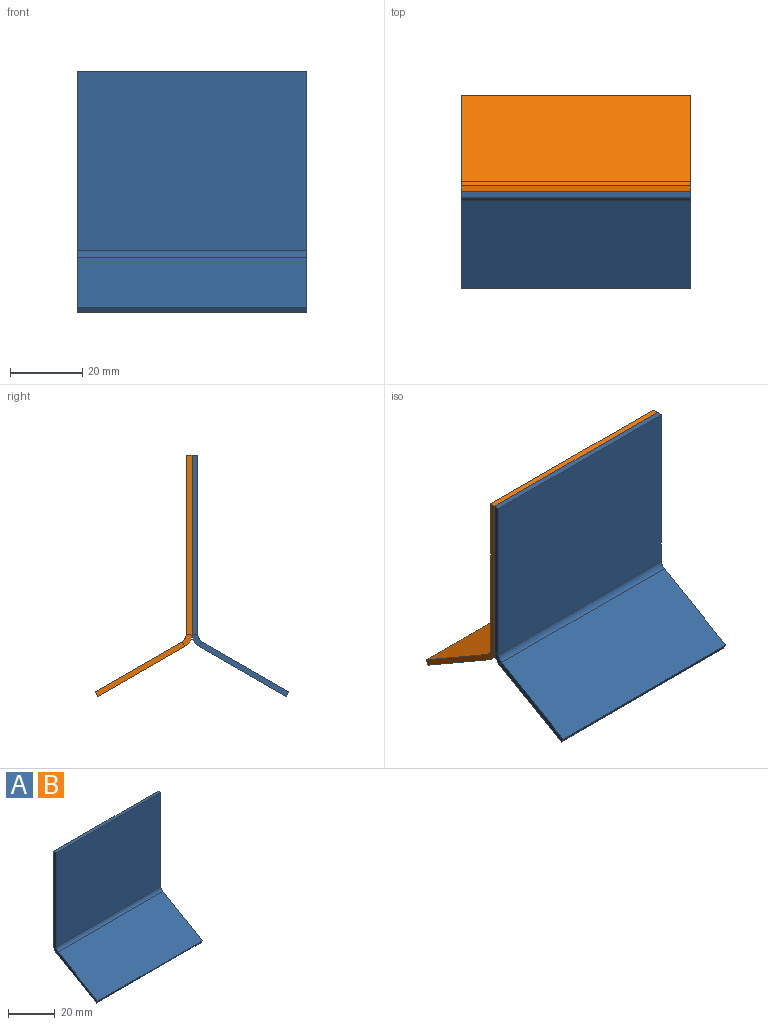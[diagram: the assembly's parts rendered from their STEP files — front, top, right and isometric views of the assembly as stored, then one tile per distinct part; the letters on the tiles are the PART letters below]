
ASSEMBLY  parts=2 mates=1
PART A: 14 faces, bbox 63.5x26.8x66.7 mm
  f0: plane 49.47x1.6mm, normal (-1,0,0), area 79.2mm2, adj f1,f3,f4,f10
  f1: plane 63.5x1.6mm, normal (0,0,1), area 101.6mm2, adj f0,f2,f3,f4
  f2: plane 49.47x1.6mm, normal (1,0,0), area 79.2mm2, adj f1,f3,f4,f11
  f3: plane 63.5x49.47mm, normal (0,1,0), area 3141.5mm2, adj f0,f1,f2,f12
  f4: plane 63.5x49.47mm, normal (0,-1,0), area 3141.5mm2, adj f0,f1,f2,f13
  f5: plane 24.83x15.26mm, normal (-1,0,0), area 44.4mm2, adj f7,f8,f9,f10
  f6: plane 24.83x15.26mm, normal (1,0,0), area 44.4mm2, adj f7,f8,f9,f11
  f7: plane 63.5x1.39mm, normal (0,-0.87,-0.5), area 101.6mm2, adj f5,f6,f8,f9
  f8: plane 63.5x24.03mm, normal (0,0.5,-0.87), area 1762mm2, adj f5,f6,f7,f12
  f9: plane 63.5x24.03mm, normal (0,-0.5,0.87), area 1762mm2, adj f5,f6,f7,f13
  f10: plane 3.38x2.75mm, normal (-1,0,0), area 5.2mm2, adj f0,f5,f12,f13
  f11: plane 3.38x2.75mm, normal (1,0,0), area 5.2mm2, adj f2,f6,f12,f13
  f12: cylinder r=3.9mm len=63.5mm, axis (-1,0,0), area 259.3mm2, adj f3,f8,f10,f11
  f13: cylinder r=2.3mm len=63.5mm, axis (-1,0,0), area 152.9mm2, adj f4,f9,f10,f11
PART B: same geometry as A
PLACE A at identity fixed
PLACE B rot(axis=(0,0,1),180deg) t=(-63.5,0,0)mm
MATE fastened B.f3 <-> A.f3  axis (0,-1,0) through (-31.75,0,26.06)mm
